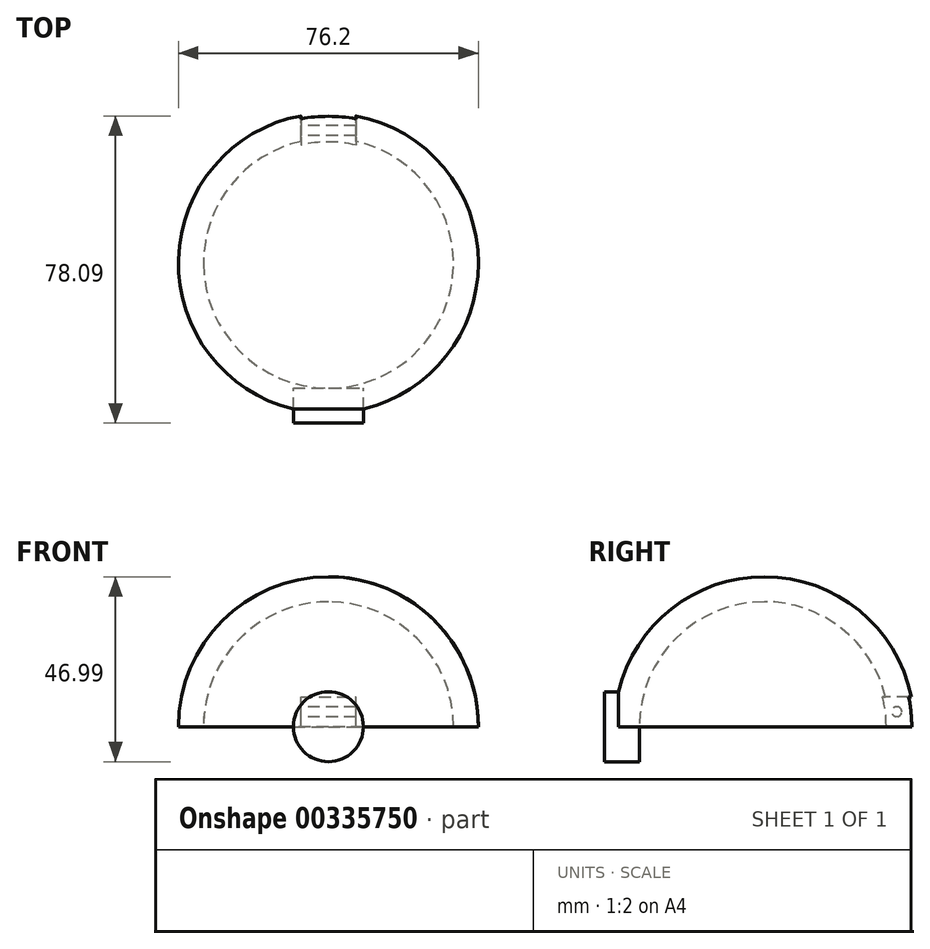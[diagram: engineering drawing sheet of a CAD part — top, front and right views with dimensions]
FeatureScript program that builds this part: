
annotation { "Feature Type Name" : "Feature", "Feature Type Description" : "" }
export const myFeature = defineFeature(function(context is Context, id is Id, definition is map)
    precondition{}
    {
        {
            var Q0;
            Q0=qCreatedBy(makeId("Front.planeOp"),FACE);
            var sketch = newSketch(context, id + "F0", { "sketchPlane" : qUnion([Q0])});
            skArc(sketch, "E0", {"start": v(0, 38.1) * mm, "mid": v(-26.94, 26.94) * mm, "end": v(-38.1, 0) * mm});
            skLineSegment(sketch, "E1", {"start": v(-38.1, 0) * mm, "end": v(-31.75, 0) * mm});
            skLineSegment(sketch, "E2", {"start": v(0, 31.75) * mm, "end": v(0, 38.1) * mm});
            skArc(sketch, "E3.0", {"start": v(0, 31.75) * mm, "mid": v(-22.45, 22.45) * mm, "end": v(-31.75, 0) * mm});
            skSolve(sketch);
        }
        {
            var Q0;
            Q0=makeQuery(id+"F0.imprint","IMPRINT",FACE,{"disambiguationData":[TD([[makeQuery(id+"F0.imprint","IMPRINT",EDGE,{"derivedFrom":sQuery(id+"F0.wireOp",EDGE,"E0")}),1.0]])]});
            var Q1;
            Q1=sQuery(id+"F0.wireOp",EDGE,"E2");
            revolve(context, id + "F1", {"entities" : qUnion([Q0]), "axis" : qUnion([Q1]), "revolveType" : RevolveType.FULL});
        }
        {
            var Q0;
            Q0=qCreatedBy(makeId("Top.planeOp"),FACE);
            var sketch = newSketch(context, id + "F2", { "sketchPlane" : qUnion([Q0])});
            skLineSegment(sketch, "E4", {"start": v(0, 0) * mm, "end": v(0, 38.1) * mm});
            skSolve(sketch);
        }
        {
            var Q0;
            Q0=qCreatedBy(makeId("Front.planeOp"),FACE);
            cPlane(context, id + "F3", {"entities" : qUnion([Q0]), "cplaneType" : CPlaneType.OFFSET, "offset" : 38.1 * mm, "width" : 152.4 * mm, "height" : 152.4 * mm});
        }
        {
            var Q0;
            Q0=qCreatedBy(id+"F3.planeOp",FACE);
            var sketch = newSketch(context, id + "F4", { "sketchPlane" : qUnion([Q0])});
            skCircle(sketch, "E5", {"center": v(0, 0) * mm, "radius": 8.9 * mm});
            skSolve(sketch);
        }
        {
            var Q0;
            Q0 = qSketchRegion(id + "F4", true);
            extrude(context, id + "F5", {"entities" : qUnion([Q0]), "operationType" : NewBodyOperationType.ADD, "depth" : 2.54 * mm, "hasSecondDirection" : true, "secondDirectionOppositeDirection" : true, "secondDirectionDepth" : 6.35 * mm});
        }
        {
            var Q0;
            Q0=qCreatedBy(makeId("Right.planeOp"),FACE);
            var sketch = newSketch(context, id + "F6", { "sketchPlane" : qUnion([Q0])});
            skLineSegment(sketch, "E6.trimOffspring", {"start": v(31.75, 0) * mm, "end": v(38.1, 0) * mm});
            skPoint(sketch, "E7.0.2.start.orphan", {"position": v(-31.75, 0) * mm});
            skPoint(sketch, "E7.0.0.start.orphan", {"position": v(-31.75, 0) * mm});
            skPoint(sketch, "E7.0.4.end.orphan", {"position": v(-37.05, 0) * mm});
            skPoint(sketch, "E7.0.5.end.orphan", {"position": v(-31.75, 0) * mm});
            skPoint(sketch, "E7.0.5.start.orphan", {"position": v(-37.05, 0) * mm});
            skCircle(sketch, "E8", {"center": v(33.65, 3.81) * mm, "radius": 1.27 * mm});
            skLineSegment(sketch, "E9", {"start": v(38.1, 0) * mm, "end": v(38.1, 7.62) * mm});
            skLineSegment(sketch, "E10", {"start": v(38.1, 7.62) * mm, "end": v(26.56, 7.62) * mm});
            skLineSegment(sketch, "E11", {"start": v(26.56, 0) * mm, "end": v(26.56, 7.62) * mm});
            skLineSegment(sketch, "E12", {"start": v(26.56, 0) * mm, "end": v(31.75, 0) * mm});
            skSolve(sketch);
        }
        {
            var Q0;
            Q0 = qSketchRegion(id + "F6", true);
            extrude(context, id + "F7", {"entities" : qUnion([Q0]), "operationType" : NewBodyOperationType.REMOVE, "endBound" : BoundingType.SYMMETRIC, "depth" : 13.97 * mm});
        }
    });
